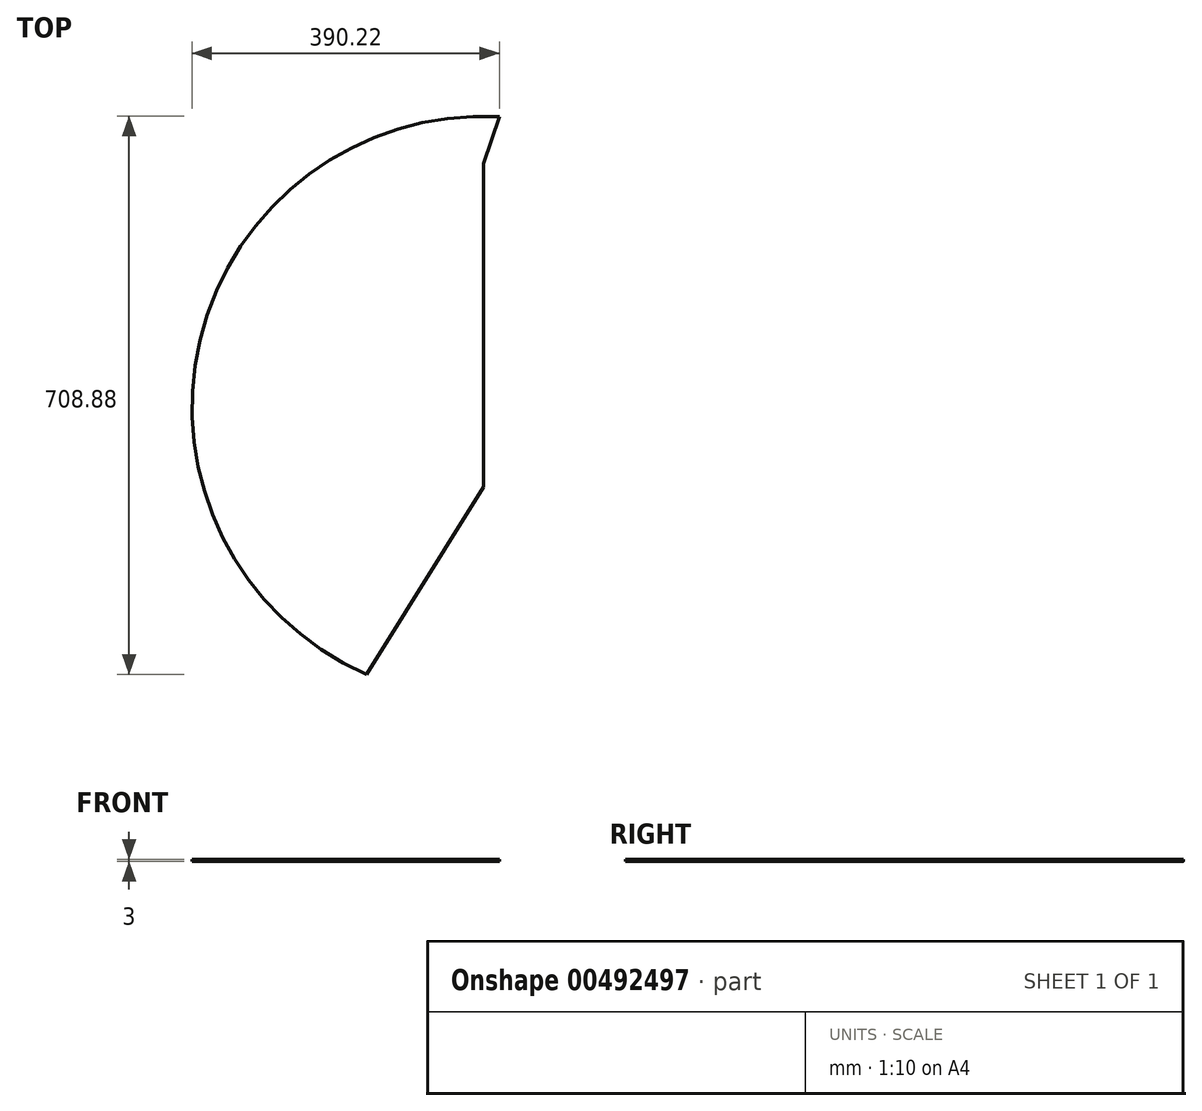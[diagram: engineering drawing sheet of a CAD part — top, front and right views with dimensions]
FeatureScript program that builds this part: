
annotation { "Feature Type Name" : "Feature", "Feature Type Description" : "" }
export const myFeature = defineFeature(function(context is Context, id is Id, definition is map)
    precondition{}
    {
        {
            var Q0;
            Q0=qCreatedBy(makeId("Top.planeOp"),FACE);
            var sketch = newSketch(context, id + "F0", { "sketchPlane" : qUnion([Q0])});
            skArc(sketch, "E0", {"start": v(2.35, 474.07) * mm, "mid": v(-377.8, 190.37) * mm, "end": v(-166.4, -234.26) * mm});
            skLineSegment(sketch, "E1", {"start": v(-17.87, 104.62) * mm, "end": v(-17.87, 414.62) * mm});
            skLineSegment(sketch, "E2", {"start": v(-17.87, 104.62) * mm, "end": v(-17.87, 3.66) * mm});
            skLineSegment(sketch, "E3", {"start": v(-17.87, 3.66) * mm, "end": v(-166.4, -234.26) * mm});
            skLineSegment(sketch, "E4", {"start": v(2.35, 474.07) * mm, "end": v(-17.87, 414.62) * mm});
            skSolve(sketch);
        }
        {
            var Q0;
            Q0 = qSketchRegion(id + "F0", true);
            extrude(context, id + "F1", {"entities" : qUnion([Q0]), "depth" : 3 * mm});
        }
    });
